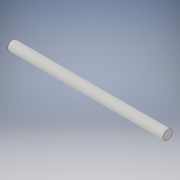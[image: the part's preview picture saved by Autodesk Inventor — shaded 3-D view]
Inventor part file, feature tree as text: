
AUTODESK INVENTOR PART (.ipt)
format: ipt  version: 2019 (Build 230136000, 136)  size: 90,112 bytes
history: native  units: in
note: dims shown in document units (in); Inventor stores cm internally (conversion verified against a paired STEP export)
features: extrude x1, sketch x1
ambient origin geometry x8: Origin, YZ Plane, XZ Plane, XY Plane, X Axis, Y Axis, Z Axis, Center Point
bodies: Solid1 (feature_tree)
feature tree (2):
  extrude  "Extrusion1"  Depth=3.937in TaperAngle=0.0deg
  sketch  "Sketch1"  dims[d0=0.2362in d1=3.937in d2=0.0in]
